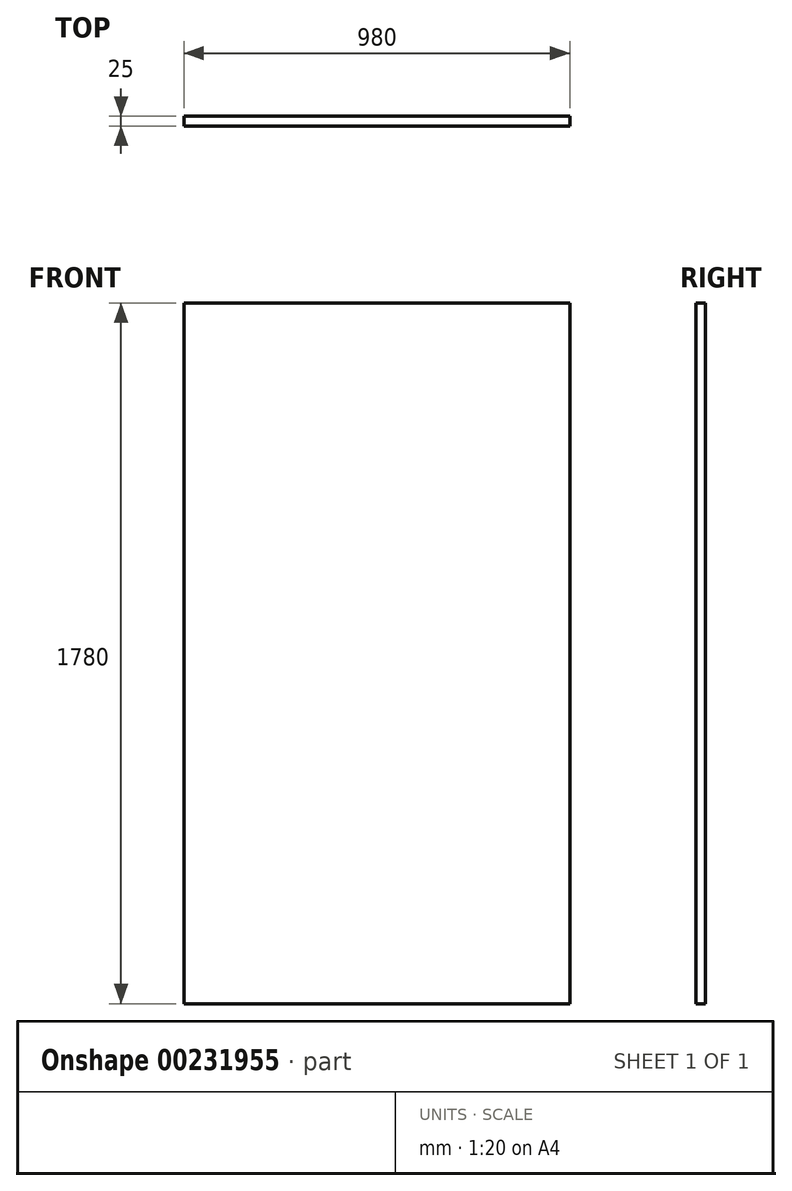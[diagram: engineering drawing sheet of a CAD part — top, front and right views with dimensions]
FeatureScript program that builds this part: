
annotation { "Feature Type Name" : "Feature", "Feature Type Description" : "" }
export const myFeature = defineFeature(function(context is Context, id is Id, definition is map)
    precondition{}
    {
        {
            var Q0;
            Q0=qCreatedBy(makeId("Front.planeOp"),FACE);
            var sketch = newSketch(context, id + "F0", { "sketchPlane" : qUnion([Q0])});
            skLineSegment(sketch, "E0.bottom", {"start": v(-490, 890) * mm, "end": v(490, 890) * mm});
            skLineSegment(sketch, "E0.top", {"start": v(-490, -890) * mm, "end": v(490, -890) * mm});
            skLineSegment(sketch, "E0.left", {"start": v(-490, 890) * mm, "end": v(-490, -890) * mm});
            skLineSegment(sketch, "E0.right", {"start": v(490, 890) * mm, "end": v(490, -890) * mm});
            skPoint(sketch, "E0.middle", {"position": v(0, 0) * mm});
            skSolve(sketch);
        }
        {
            var Q0;
            Q0 = qSketchRegion(id + "F0", true);
            extrude(context, id + "F1", {"entities" : qUnion([Q0]), "depth" : 25 * mm});
        }
    });
